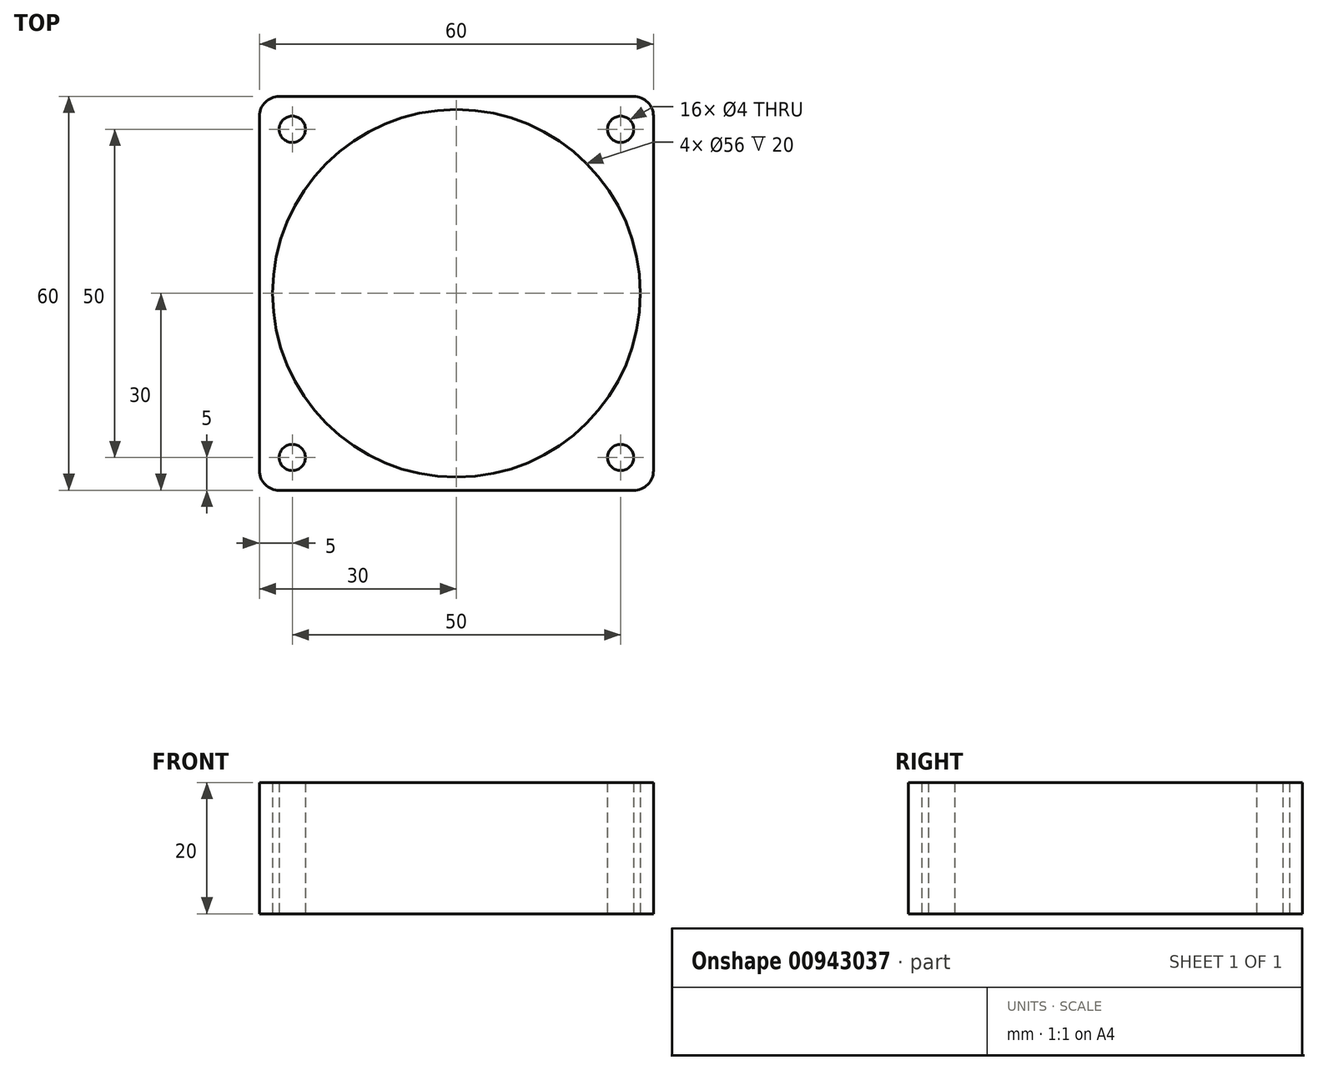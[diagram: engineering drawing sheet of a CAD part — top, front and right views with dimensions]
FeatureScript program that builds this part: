
annotation { "Feature Type Name" : "Feature", "Feature Type Description" : "" }
export const myFeature = defineFeature(function(context is Context, id is Id, definition is map)
    precondition{}
    {
        {
            var Q0;
            Q0=qCreatedBy(makeId("Top.planeOp"),FACE);
            var sketch = newSketch(context, id + "F0", { "sketchPlane" : qUnion([Q0])});
            skLineSegment(sketch, "E0.bottom", {"start": v(-27, 30) * mm, "end": v(27, 30) * mm});
            skLineSegment(sketch, "E0.top", {"start": v(-27, -30) * mm, "end": v(27, -30) * mm});
            skLineSegment(sketch, "E0.left", {"start": v(-30, 27) * mm, "end": v(-30, -27) * mm});
            skLineSegment(sketch, "E0.right", {"start": v(30, 27) * mm, "end": v(30, -27) * mm});
            skLineSegment(sketch, "E1.bottom", {"start": v(-25, 25) * mm, "end": v(25, 25) * mm, "construction": true});
            skLineSegment(sketch, "E1.top", {"start": v(-25, -25) * mm, "end": v(25, -25) * mm, "construction": true});
            skLineSegment(sketch, "E1.left", {"start": v(-25, 25) * mm, "end": v(-25, -25) * mm, "construction": true});
            skLineSegment(sketch, "E1.right", {"start": v(25, 25) * mm, "end": v(25, -25) * mm, "construction": true});
            skCircle(sketch, "E2", {"center": v(0, 0) * mm, "radius": 28 * mm});
            skPoint(sketch, "E3.visualSharp", {"position": v(-30, 30) * mm});
            skArc(sketch, "E3.filletArc", {"start": v(-27, 30) * mm, "mid": v(-29.12, 29.12) * mm, "end": v(-30, 27) * mm});
            skPoint(sketch, "E4.visualSharp", {"position": v(30, 30) * mm});
            skArc(sketch, "E4.filletArc", {"start": v(30, 27) * mm, "mid": v(29.12, 29.12) * mm, "end": v(27, 30) * mm});
            skPoint(sketch, "E5.visualSharp", {"position": v(30, -30) * mm});
            skArc(sketch, "E5.filletArc", {"start": v(27, -30) * mm, "mid": v(29.12, -29.12) * mm, "end": v(30, -27) * mm});
            skPoint(sketch, "E6.visualSharp", {"position": v(-30, -30) * mm});
            skArc(sketch, "E6.filletArc", {"start": v(-30, -27) * mm, "mid": v(-29.12, -29.12) * mm, "end": v(-27, -30) * mm});
            skCircle(sketch, "E7", {"center": v(-25, 25) * mm, "radius": 2 * mm});
            skCircle(sketch, "E8", {"center": v(25, 25) * mm, "radius": 2 * mm});
            skCircle(sketch, "E9", {"center": v(25, -25) * mm, "radius": 2 * mm});
            skCircle(sketch, "E10", {"center": v(-25, -25) * mm, "radius": 2 * mm});
            skSolve(sketch);
        }
        {
            var Q0;
            Q0=makeQuery(id+"F0.imprint","IMPRINT",FACE,{"disambiguationData":[TD([[makeQuery(id+"F0.imprint","IMPRINT",EDGE,{"derivedFrom":sQuery(id+"F0.wireOp",EDGE,"E0.bottom")}),-1.0]])]});
            extrude(context, id + "F1", {"entities" : qUnion([Q0]), "depth" : 20 * mm, "offsetDistance" : 25 * mm});
        }
    });
